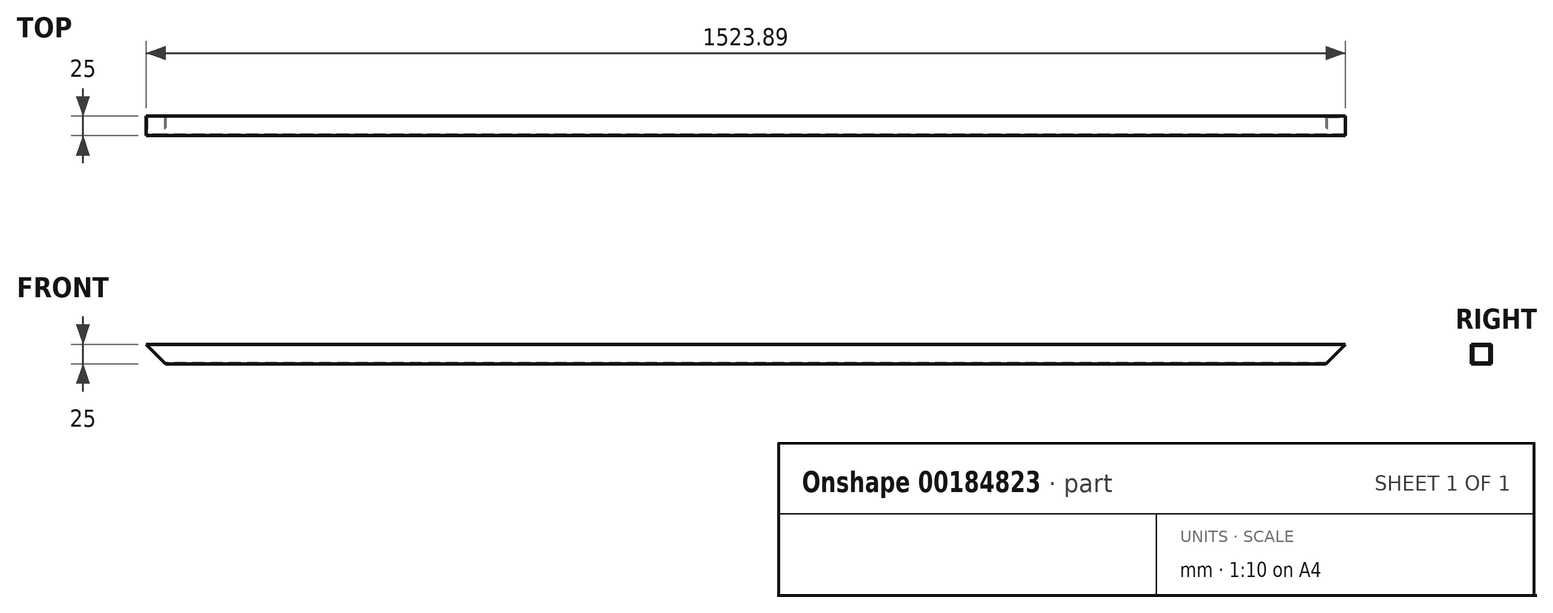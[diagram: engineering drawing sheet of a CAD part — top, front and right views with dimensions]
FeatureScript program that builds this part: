
annotation { "Feature Type Name" : "Feature", "Feature Type Description" : "" }
export const myFeature = defineFeature(function(context is Context, id is Id, definition is map)
    precondition{}
    {
        {
            var Q0;
            Q0=qCreatedBy(makeId("Right.planeOp"),FACE);
            var sketch = newSketch(context, id + "F0", { "sketchPlane" : qUnion([Q0])});
            skLineSegment(sketch, "E0.bottom", {"start": v(12.5, 12.5) * mm, "end": v(-12.5, 12.5) * mm});
            skLineSegment(sketch, "E0.top", {"start": v(12.5, -12.5) * mm, "end": v(-12.5, -12.5) * mm});
            skLineSegment(sketch, "E0.left", {"start": v(12.5, 12.5) * mm, "end": v(12.5, -12.5) * mm});
            skLineSegment(sketch, "E0.right", {"start": v(-12.5, 12.5) * mm, "end": v(-12.5, -12.5) * mm});
            skPoint(sketch, "E0.middle", {"position": v(0, 0) * mm});
            skSolve(sketch);
        }
        {
            var Q0;
            Q0=qSketchRegion(id+"F0",true);
            extrude(context, id + "F1", {"entities" : qUnion([Q0]), "depth" : 1524 * mm});
        }
        {
            var Q0;
            Q0=qCreatedBy(makeId("Front.planeOp"),FACE);
            var sketch = newSketch(context, id + "F2", { "sketchPlane" : qUnion([Q0])});
            skLineSegment(sketch, "E1", {"start": v(0, 12.6) * mm, "end": v(35.35, -22.75) * mm});
            skLineSegment(sketch, "E2", {"start": v(1524, 12.5) * mm, "end": v(1494.64, -16.86) * mm});
            skLineSegment(sketch, "E3", {"start": v(0, 12.6) * mm, "end": v(0, -26.69) * mm});
            skLineSegment(sketch, "E4", {"start": v(0, -26.69) * mm, "end": v(35.35, -22.75) * mm});
            skLineSegment(sketch, "E5", {"start": v(1524, 12.5) * mm, "end": v(1524, -22.75) * mm});
            skLineSegment(sketch, "E6", {"start": v(1524, -22.75) * mm, "end": v(1494.64, -16.86) * mm});
            skSolve(sketch);
        }
        {
            var Q0;
            Q0=makeQuery(id+"F2.imprint","IMPRINT",FACE,{"disambiguationData":[TD([[makeQuery(id+"F2.imprint","IMPRINT",EDGE,{"derivedFrom":sQuery(id+"F2.wireOp",EDGE,"E1")}),-1.0]])]});
            var Q1;
            Q1=makeQuery(id+"F2.imprint","IMPRINT",FACE,{"disambiguationData":[TD([[makeQuery(id+"F2.imprint","IMPRINT",EDGE,{"derivedFrom":sQuery(id+"F2.wireOp",EDGE,"E2")}),1.0]])]});
            extrude(context, id + "F3", {"entities" : qUnion([Q0, Q1]), "operationType" : NewBodyOperationType.REMOVE, "endBound" : BoundingType.SYMMETRIC, "depth" : 25 * mm});
        }
        {
            var Q0;
            Q0=qCreatedBy(makeId("Right.planeOp"),FACE);
            var sketch = newSketch(context, id + "F4", { "sketchPlane" : qUnion([Q0])});
            skLineSegment(sketch, "E7.bottom", {"start": v(-11, 11) * mm, "end": v(11, 11) * mm});
            skLineSegment(sketch, "E7.top", {"start": v(-11, -11) * mm, "end": v(11, -11) * mm});
            skLineSegment(sketch, "E7.left", {"start": v(-11, 11) * mm, "end": v(-11, -11) * mm});
            skLineSegment(sketch, "E7.right", {"start": v(11, 11) * mm, "end": v(11, -11) * mm});
            skPoint(sketch, "E7.middle", {"position": v(0, 0) * mm});
            skSolve(sketch);
        }
        {
            var Q0;
            Q0=makeQuery(id+"F4.imprint","IMPRINT",FACE,{"disambiguationData":[TD([[makeQuery(id+"F4.imprint","IMPRINT",EDGE,{"derivedFrom":sQuery(id+"F4.wireOp",EDGE,"E7.bottom")}),-1.0]])]});
            var Q1;
            Q1=makeQuery(id+"F3.boolean.opBoolean","COPY",FACE,{"derivedFrom":makeQuery(id+"F3.opExtrude","SWEPT_FACE",FACE,{"disambiguationData":[OSD([sQuery(id+"F2.wireOp",EDGE,"E2")])]})});
            extrude(context, id + "F5", {"entities" : qUnion([Q0]), "operationType" : NewBodyOperationType.REMOVE, "endBound" : BoundingType.THROUGH_ALL, "endBoundEntityFace" : qUnion([Q1]), "depth" : 750 * mm});
        }
    });
